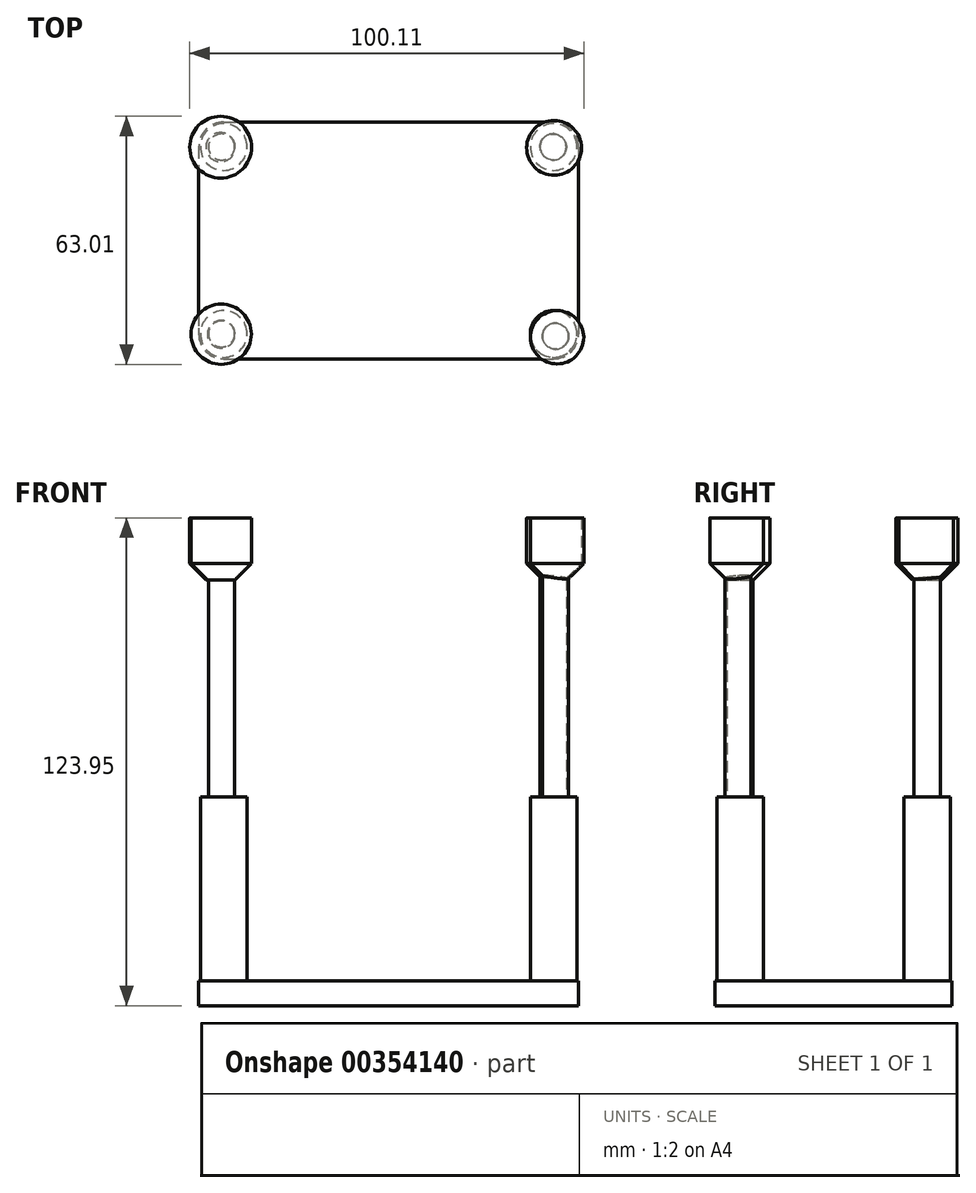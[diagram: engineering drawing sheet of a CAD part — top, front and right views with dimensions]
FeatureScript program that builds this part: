
annotation { "Feature Type Name" : "Feature", "Feature Type Description" : "" }
export const myFeature = defineFeature(function(context is Context, id is Id, definition is map)
    precondition{}
    {
        {
            var Q0;
            Q0=qCreatedBy(makeId("Top.planeOp"),FACE);
            var sketch = newSketch(context, id + "F0", { "sketchPlane" : qUnion([Q0])});
            skLineSegment(sketch, "E0.bottom", {"start": v(-66.8, 9.4) * mm, "end": v(17.03, 9.4) * mm});
            skLineSegment(sketch, "E0.top", {"start": v(-66.8, -50.8) * mm, "end": v(17.03, -50.8) * mm});
            skLineSegment(sketch, "E0.left", {"start": v(-73.14, 3.05) * mm, "end": v(-73.14, -44.44) * mm});
            skLineSegment(sketch, "E0.right", {"start": v(23.38, 3.05) * mm, "end": v(23.38, -44.44) * mm});
            skPoint(sketch, "E1.visualSharp", {"position": v(-73.14, 9.4) * mm});
            skArc(sketch, "E1.filletArc", {"start": v(-66.8, 9.4) * mm, "mid": v(-71.28, 7.54) * mm, "end": v(-73.14, 3.05) * mm});
            skPoint(sketch, "E2.visualSharp", {"position": v(23.38, 9.4) * mm});
            skArc(sketch, "E2.filletArc", {"start": v(23.38, 3.05) * mm, "mid": v(21.52, 7.54) * mm, "end": v(17.03, 9.4) * mm});
            skPoint(sketch, "E3.visualSharp", {"position": v(23.38, -50.8) * mm});
            skArc(sketch, "E3.filletArc", {"start": v(17.03, -50.8) * mm, "mid": v(21.52, -48.93) * mm, "end": v(23.38, -44.44) * mm});
            skPoint(sketch, "E4.visualSharp", {"position": v(-73.14, -50.8) * mm});
            skArc(sketch, "E4.filletArc", {"start": v(-73.14, -44.44) * mm, "mid": v(-71.28, -48.93) * mm, "end": v(-66.8, -50.8) * mm});
            skSolve(sketch);
        }
        {
            var Q0;
            Q0 = qSketchRegion(id + "F0", true);
            extrude(context, id + "F1", {"entities" : qUnion([Q0]), "depth" : 6.35 * mm});
        }
        {
            var Q0;
            Q0=makeQuery(id+"F1.opExtrude","CAP_FACE",FACE,{"disambiguationData":[OSD([sQuery(id+"F0.wireOp",EDGE,"E0.bottom"),sQuery(id+"F0.wireOp",EDGE,"E0.top"),sQuery(id+"F0.wireOp",EDGE,"E0.left"),sQuery(id+"F0.wireOp",EDGE,"E0.right"),sQuery(id+"F0.wireOp",EDGE,"E1.filletArc"),sQuery(id+"F0.wireOp",EDGE,"E2.filletArc"),sQuery(id+"F0.wireOp",EDGE,"E3.filletArc"),sQuery(id+"F0.wireOp",EDGE,"E4.filletArc")])],"isStart":false});
            var sketch = newSketch(context, id + "F2", { "sketchPlane" : qUnion([Q0])});
            skCircle(sketch, "E5", {"center": v(-66.8, 3.05) * mm, "radius": 5.95 * mm});
            skCircle(sketch, "E6", {"center": v(17.03, 3.05) * mm, "radius": 5.95 * mm});
            skCircle(sketch, "E7", {"center": v(-66.8, -44.44) * mm, "radius": 5.95 * mm});
            skCircle(sketch, "E8", {"center": v(17.03, -44.44) * mm, "radius": 5.95 * mm});
            skSolve(sketch);
        }
        {
            var Q0;
            Q0 = qSketchRegion(id + "F2", true);
            extrude(context, id + "F3", {"entities" : qUnion([Q0]), "operationType" : NewBodyOperationType.ADD, "depth" : 46.74 * mm});
        }
        {
            var Q0;
            Q0=qCreatedBy(makeId("Top.planeOp"),FACE);
            var sketch = newSketch(context, id + "F4", { "sketchPlane" : qUnion([Q0])});
            skCircle(sketch, "E9", {"center": v(-67.33, 3.06) * mm, "radius": 3.32 * mm});
            skCircle(sketch, "E10", {"center": v(16.9, 3.06) * mm, "radius": 3.32 * mm});
            skCircle(sketch, "E11", {"center": v(-67.33, -44.45) * mm, "radius": 3.32 * mm});
            skCircle(sketch, "E12", {"center": v(17.49, -45.03) * mm, "radius": 3.32 * mm});
            skSolve(sketch);
        }
        {
            var Q0;
            Q0 = qSketchRegion(id + "F4", true);
            extrude(context, id + "F5", {"entities" : qUnion([Q0]), "operationType" : NewBodyOperationType.ADD, "depth" : 110.24 * mm});
        }
        {
            var Q0;
            Q0=qCreatedBy(makeId("Top.planeOp"),FACE);
            var sketch = newSketch(context, id + "F6", { "sketchPlane" : qUnion([Q0])});
            skCircle(sketch, "E13", {"center": v(-67.6, 3) * mm, "radius": 7.85 * mm});
            skCircle(sketch, "E14", {"center": v(-67.44, -44.52) * mm, "radius": 7.65 * mm});
            skCircle(sketch, "E15", {"center": v(17.12, 2.84) * mm, "radius": 6.96 * mm});
            skCircle(sketch, "E16", {"center": v(17.9, -45.3) * mm, "radius": 6.76 * mm});
            skSolve(sketch);
        }
        {
            var Q0;
            Q0 = qSketchRegion(id + "F6", true);
            extrude(context, id + "F7", {"entities" : qUnion([Q0]), "operationType" : NewBodyOperationType.ADD, "depth" : 123.95 * mm, "hasSecondDirection" : true, "secondDirectionOppositeDirection" : false, "secondDirectionDepth" : 108.2 * mm});
        }
        {
            var Q0;
            Q0=makeQuery(id+"F7.opExtrude","CAP_EDGE",EDGE,{"disambiguationData":[OSD([sQuery(id+"F6.wireOp",EDGE,"E14")])],"isStart":true});
            var Q1;
            Q1=makeQuery(id+"F7.opExtrude","CAP_EDGE",EDGE,{"disambiguationData":[OSD([sQuery(id+"F6.wireOp",EDGE,"E13")])],"isStart":true});
            var Q2;
            Q2=makeQuery(id+"F7.opExtrude","CAP_EDGE",EDGE,{"disambiguationData":[OSD([sQuery(id+"F6.wireOp",EDGE,"E16")])],"isStart":true});
            var Q3;
            Q3=makeQuery(id+"F7.opExtrude","CAP_EDGE",EDGE,{"disambiguationData":[OSD([sQuery(id+"F6.wireOp",EDGE,"E15")])],"isStart":true});
            chamfer(context, id + "F8", {"entities" : qUnion([Q0, Q1, Q2, Q3]), "width" : 4.14 * mm, "tangentPropagation" : true});
        }
    });
